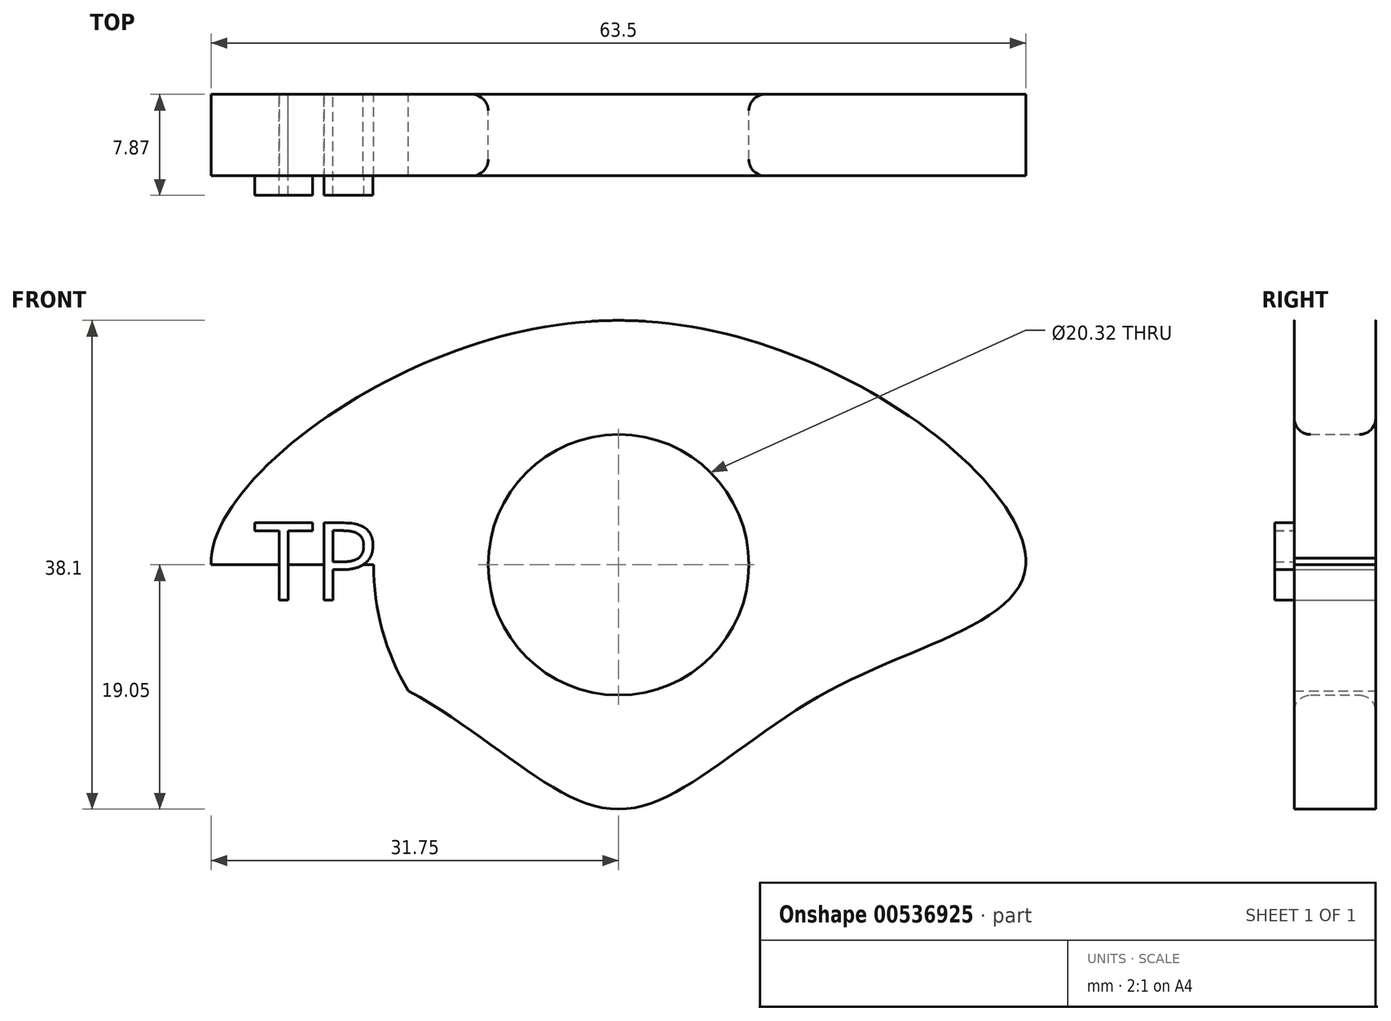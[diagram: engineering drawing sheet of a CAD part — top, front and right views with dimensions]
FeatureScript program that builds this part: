
annotation { "Feature Type Name" : "Feature", "Feature Type Description" : "" }
export const myFeature = defineFeature(function(context is Context, id is Id, definition is map)
    precondition{}
    {
        {
            var Q0;
            Q0=qCreatedBy(makeId("Front.planeOp"),FACE);
            var sketch = newSketch(context, id + "F0", { "sketchPlane" : qUnion([Q0])});
            skLineSegment(sketch, "E0.bottom", {"start": v(0, 0) * mm, "end": v(-63.5, 0) * mm});
            skLineSegment(sketch, "E0.top", {"start": v(0, -38.1) * mm, "end": v(-63.5, -38.1) * mm});
            skLineSegment(sketch, "E0.left", {"start": v(0, 0) * mm, "end": v(0, -38.1) * mm});
            skLineSegment(sketch, "E0.right", {"start": v(-63.5, 0) * mm, "end": v(-63.5, -38.1) * mm});
            skLineSegment(sketch, "E1", {"start": v(-63.5, 0) * mm, "end": v(0, -38.1) * mm});
            skLineSegment(sketch, "E2", {"start": v(0, 0) * mm, "end": v(-63.5, -38.1) * mm});
            skLineSegment(sketch, "E3", {"start": v(-63.5, -19.05) * mm, "end": v(0, -19.05) * mm});
            skLineSegment(sketch, "E4", {"start": v(-31.75, 0) * mm, "end": v(-31.75, -38.1) * mm});
            skCircle(sketch, "E5", {"center": v(-31.75, -19.05) * mm, "radius": 10.16 * mm});
            skCircle(sketch, "E6", {"center": v(-31.75, -19.05) * mm, "radius": 19.1 * mm});
            skFitSpline(sketch, "E7", {"points": [v(-63.5, -19.05) * mm, v(-48.13, -28.88) * mm, v(-31.75, -38.1) * mm, v(-15.37, -28.88) * mm, v(0, -19.05) * mm, v(-31.75, 0) * mm, v(-63.5, -19.05) * mm]});
            skSolve(sketch);
        }
        {
            var Q0;
            {var subQ0=sQuery(id+"F0.wireOp",EDGE,"E5");var subQ1=sQuery(id+"F0.wireOp",EDGE,"E1");var subQ2=makeQuery(id+"F0.imprint","INTERSECT",VERTEX,{"disambiguationData":[OD(1.0)],"derivedFrom":[subQ1,subQ0]});Q0=makeQuery(id+"F0.imprint","IMPRINT",FACE,{"disambiguationData":[TD([[makeQuery(id+"F0.imprint","IMPRINT",EDGE,{"disambiguationData":[TD([[subQ2,1.0]])],"derivedFrom":subQ0}),-1.0]])]});}
            var Q1;
            {var subQ0=sQuery(id+"F0.wireOp",EDGE,"E5");var subQ5=sQuery(id+"F0.wireOp",EDGE,"E3");var subQ6=makeQuery(id+"F0.imprint","INTERSECT",VERTEX,{"disambiguationData":[OD(1.0)],"derivedFrom":[subQ5,subQ0]});Q1=makeQuery(id+"F0.imprint","IMPRINT",FACE,{"disambiguationData":[TD([[makeQuery(id+"F0.imprint","IMPRINT",EDGE,{"disambiguationData":[TD([[subQ6,-1.0]])],"derivedFrom":subQ5}),-1.0]])]});}
            var Q2;
            {var subQ1=sQuery(id+"F0.wireOp",EDGE,"E3");var subQ3=sQuery(id+"F0.wireOp",EDGE,"E6");var subQ4=makeQuery(id+"F0.imprint","INTERSECT",VERTEX,{"disambiguationData":[OD(1.0)],"derivedFrom":[subQ1,subQ3]});Q2=makeQuery(id+"F0.imprint","IMPRINT",FACE,{"disambiguationData":[TD([[makeQuery(id+"F0.imprint","IMPRINT",EDGE,{"disambiguationData":[TD([[subQ4,-1.0]])],"derivedFrom":subQ1}),-1.0]])]});}
            var Q3;
            {var subQ1=sQuery(id+"F0.wireOp",EDGE,"E2");var subQ5=sQuery(id+"F0.wireOp",EDGE,"E7");var subQ8=makeQuery(id+"F0.imprint","INTERSECT",VERTEX,{"derivedFrom":[subQ1,subQ5]});Q3=makeQuery(id+"F0.imprint","IMPRINT",FACE,{"disambiguationData":[TD([[makeQuery(id+"F0.imprint","IMPRINT",EDGE,{"disambiguationData":[TD([[subQ8,-1.0]])],"derivedFrom":subQ1}),1.0]])]});}
            var Q4;
            {var subQ0=sQuery(id+"F0.wireOp",EDGE,"E6");var subQ1=sQuery(id+"F0.wireOp",EDGE,"E2");var subQ2=makeQuery(id+"F0.imprint","INTERSECT",VERTEX,{"derivedFrom":[subQ1,subQ0]});Q4=makeQuery(id+"F0.imprint","IMPRINT",FACE,{"disambiguationData":[TD([[makeQuery(id+"F0.imprint","IMPRINT",EDGE,{"disambiguationData":[TD([[subQ2,-1.0]])],"derivedFrom":subQ1}),1.0]])]});}
            var Q5;
            {var subQ0=sQuery(id+"F0.wireOp",EDGE,"E6");var subQ1=sQuery(id+"F0.wireOp",EDGE,"E2");var subQ2=makeQuery(id+"F0.imprint","INTERSECT",VERTEX,{"derivedFrom":[subQ1,subQ0]});Q5=makeQuery(id+"F0.imprint","IMPRINT",FACE,{"disambiguationData":[TD([[makeQuery(id+"F0.imprint","IMPRINT",EDGE,{"disambiguationData":[TD([[subQ2,-1.0]])],"derivedFrom":subQ1}),-1.0]])]});}
            var Q6;
            {var subQ1=sQuery(id+"F0.wireOp",EDGE,"E1");var subQ5=sQuery(id+"F0.wireOp",EDGE,"E6");var subQ6=makeQuery(id+"F0.imprint","INTERSECT",VERTEX,{"derivedFrom":[subQ1,subQ5]});Q6=makeQuery(id+"F0.imprint","IMPRINT",FACE,{"disambiguationData":[TD([[makeQuery(id+"F0.imprint","IMPRINT",EDGE,{"disambiguationData":[TD([[subQ6,-1.0]])],"derivedFrom":subQ1}),1.0]])]});}
            var Q7;
            {var subQ0=sQuery(id+"F0.wireOp",EDGE,"E7");var subQ6=sQuery(id+"F0.wireOp",EDGE,"E1");var subQ7=makeQuery(id+"F0.imprint","INTERSECT",VERTEX,{"derivedFrom":[subQ6,subQ0]});Q7=makeQuery(id+"F0.imprint","IMPRINT",FACE,{"disambiguationData":[TD([[makeQuery(id+"F0.imprint","IMPRINT",EDGE,{"disambiguationData":[TD([[subQ7,-1.0]])],"derivedFrom":subQ6}),-1.0]])]});}
            var Q8;
            {var subQ1=sQuery(id+"F0.wireOp",EDGE,"E3");var subQ3=sQuery(id+"F0.wireOp",EDGE,"E6");var subQ4=makeQuery(id+"F0.imprint","INTERSECT",VERTEX,{"disambiguationData":[OD(0.0)],"derivedFrom":[subQ1,subQ3]});Q8=makeQuery(id+"F0.imprint","IMPRINT",FACE,{"disambiguationData":[TD([[makeQuery(id+"F0.imprint","IMPRINT",EDGE,{"disambiguationData":[TD([[subQ4,1.0]])],"derivedFrom":subQ1}),-1.0]])]});}
            var Q9;
            {var subQ3=sQuery(id+"F0.wireOp",EDGE,"E6");var subQ5=sQuery(id+"F0.wireOp",EDGE,"E3");var subQ6=makeQuery(id+"F0.imprint","INTERSECT",VERTEX,{"disambiguationData":[OD(0.0)],"derivedFrom":[subQ5,subQ3]});Q9=makeQuery(id+"F0.imprint","IMPRINT",FACE,{"disambiguationData":[TD([[makeQuery(id+"F0.imprint","IMPRINT",EDGE,{"disambiguationData":[TD([[subQ6,-1.0]])],"derivedFrom":subQ5}),-1.0]])]});}
            var Q10;
            {var subQ0=sQuery(id+"F0.wireOp",EDGE,"E6");var subQ1=sQuery(id+"F0.wireOp",EDGE,"E1");var subQ2=makeQuery(id+"F0.imprint","INTERSECT",VERTEX,{"derivedFrom":[subQ1,subQ0]});Q10=makeQuery(id+"F0.imprint","IMPRINT",FACE,{"disambiguationData":[TD([[makeQuery(id+"F0.imprint","IMPRINT",EDGE,{"disambiguationData":[TD([[subQ2,-1.0]])],"derivedFrom":subQ1}),-1.0]])]});}
            var Q11;
            {var subQ0=sQuery(id+"F0.wireOp",EDGE,"E5");var subQ1=sQuery(id+"F0.wireOp",EDGE,"E2");var subQ2=makeQuery(id+"F0.imprint","INTERSECT",VERTEX,{"disambiguationData":[OD(1.0)],"derivedFrom":[subQ1,subQ0]});Q11=makeQuery(id+"F0.imprint","IMPRINT",FACE,{"disambiguationData":[TD([[makeQuery(id+"F0.imprint","IMPRINT",EDGE,{"disambiguationData":[TD([[subQ2,-1.0]])],"derivedFrom":subQ0}),-1.0]])]});}
            var Q12;
            {var subQ0=sQuery(id+"F0.wireOp",EDGE,"E7");var subQ1=sQuery(id+"F0.wireOp",EDGE,"E2");var subQ2=makeQuery(id+"F0.imprint","INTERSECT",VERTEX,{"derivedFrom":[subQ1,subQ0]});Q12=makeQuery(id+"F0.imprint","IMPRINT",FACE,{"disambiguationData":[TD([[makeQuery(id+"F0.imprint","IMPRINT",EDGE,{"disambiguationData":[TD([[subQ2,-1.0]])],"derivedFrom":subQ1}),-1.0]])]});}
            var Q13;
            {var subQ0=sQuery(id+"F0.wireOp",EDGE,"E7");var subQ1=sQuery(id+"F0.wireOp",EDGE,"E1");var subQ2=makeQuery(id+"F0.imprint","INTERSECT",VERTEX,{"derivedFrom":[subQ1,subQ0]});Q13=makeQuery(id+"F0.imprint","IMPRINT",FACE,{"disambiguationData":[TD([[makeQuery(id+"F0.imprint","IMPRINT",EDGE,{"disambiguationData":[TD([[subQ2,-1.0]])],"derivedFrom":subQ1}),1.0]])]});}
            extrude(context, id + "F1", {"entities" : qUnion([Q0, Q1, Q2, Q3, Q4, Q5, Q6, Q7, Q8, Q9, Q10, Q11, Q12, Q13]), "depth" : 6.35 * mm, "offsetDistance" : 25.4 * mm});
        }
        {
            var Q0;
            Q0=makeQuery(id+"F1.opExtrude","CAP_EDGE",EDGE,{"disambiguationData":[OSD([sQuery(id+"F0.wireOp",EDGE,"E5")])],"isStart":false});
            var Q1;
            Q1=makeQuery(id+"F1.opExtrude","CAP_EDGE",EDGE,{"disambiguationData":[OSD([sQuery(id+"F0.wireOp",EDGE,"E5")])],"isStart":true});
            fillet(context, id + "F2", {"entities" : qUnion([Q0, Q1]), "radius" : 1.27 * mm, "tangentPropagation" : true, "allowEdgeOverflow" : false});
        }
        {
            var Q0;
            Q0=qCreatedBy(makeId("Front.planeOp"),FACE);
            var sketch = newSketch(context, id + "F3", { "sketchPlane" : qUnion([Q0])});
            skText(sketch, "E8", { "text": "TP", "fontName": "OpenSans-Regular.ttf"});
            const initialGuessF3  = {"E8": [-0.06018, -0.02179, 1, 0, 0.00606]};
            skSetInitialGuess(sketch, initialGuessF3);
            skSolve(sketch);
        }
        {
            var Q0;
            Q0 = qSketchRegion(id + "F3", true);
            extrude(context, id + "F4", {"entities" : qUnion([Q0]), "operationType" : NewBodyOperationType.ADD, "depth" : 7.87 * mm, "offsetDistance" : 25.4 * mm});
        }
    });
